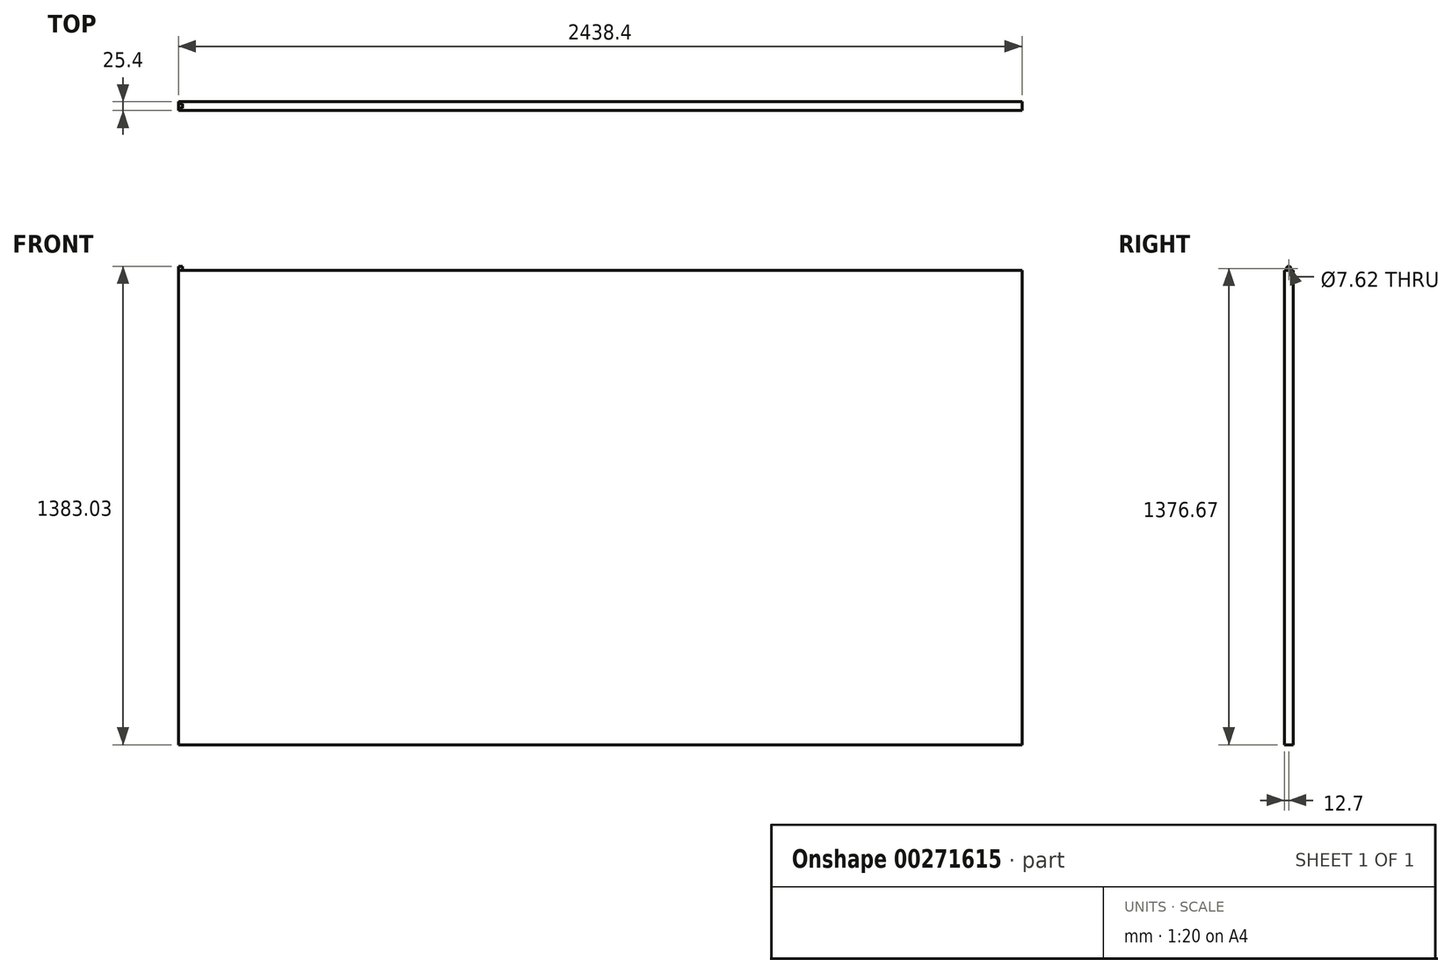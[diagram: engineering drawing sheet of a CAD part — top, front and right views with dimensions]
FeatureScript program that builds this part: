
annotation { "Feature Type Name" : "Feature", "Feature Type Description" : "" }
export const myFeature = defineFeature(function(context is Context, id is Id, definition is map)
    precondition{}
    {
        {
            var Q0;
            Q0=qCreatedBy(makeId("Front.planeOp"),FACE);
            var sketch = newSketch(context, id + "F0", { "sketchPlane" : qUnion([Q0])});
            skLineSegment(sketch, "E0.bottom", {"start": v(-904.05, 1352.8) * mm, "end": v(1534.35, 1352.8) * mm});
            skLineSegment(sketch, "E0.top", {"start": v(-904.05, -18.8) * mm, "end": v(1534.35, -18.8) * mm});
            skLineSegment(sketch, "E0.left", {"start": v(-904.05, 1352.8) * mm, "end": v(-904.05, -18.8) * mm});
            skLineSegment(sketch, "E0.right", {"start": v(1534.35, 1352.8) * mm, "end": v(1534.35, -18.8) * mm});
            skSolve(sketch);
        }
        {
            var Q0;
            Q0=makeQuery(id+"F0.imprint","IMPRINT",FACE,{"disambiguationData":[TD([[makeQuery(id+"F0.imprint","IMPRINT",EDGE,{"derivedFrom":sQuery(id+"F0.wireOp",EDGE,"E0.bottom")}),-1.0]])]});
            extrude(context, id + "F1", {"entities" : qUnion([Q0]), "depth" : 25.4 * mm, "offsetDistance" : 25.4 * mm});
        }
        {
            var Q0;
            Q0=makeQuery(id+"F1.opExtrude","SWEPT_FACE",FACE,{"disambiguationData":[OSD([sQuery(id+"F0.wireOp",EDGE,"E0.left")])]});
            var sketch = newSketch(context, id + "F2", { "sketchPlane" : qUnion([Q0])});
            skCircle(sketch, "E1", {"center": v(12.7, 1357.89) * mm, "radius": 3.81 * mm});
            skArc(sketch, "E2", {"start": v(16.51, 1352.8) * mm, "mid": v(12.7, 1364.24) * mm, "end": v(8.89, 1352.8) * mm});
            skSolve(sketch);
        }
        {
            var Q0;
            Q0=makeQuery(id+"F2.imprint","IMPRINT",FACE,{"disambiguationData":[TD([[makeQuery(id+"F2.imprint","IMPRINT",EDGE,{"derivedFrom":sQuery(id+"F2.wireOp",EDGE,"E1")}),-1.0]])]});
            extrude(context, id + "F3", {"entities" : qUnion([Q0]), "depth" : -12.7 * mm, "offsetDistance" : 25.4 * mm});
        }
    });
